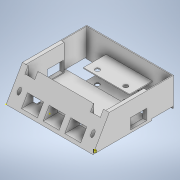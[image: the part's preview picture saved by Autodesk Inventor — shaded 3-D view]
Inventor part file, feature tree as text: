
AUTODESK INVENTOR PART (.ipt)
format: ipt  version: 2021 (Build 250183000, 183)  size: 445,952 bytes
history: native  units: mm
features: sketch x23, extrude x19, projected_geometry x2, other x1
ambient origin geometry x8: Origin, YZ Plane, XZ Plane, XY Plane, X Axis, Y Axis, Z Axis, Center Point
bodies: Body1 (feature_tree)
feature tree (45):
  other  "Sólido1"
  extrude  "Extrusion Base"  Depth=2.0mm TaperAngle=0.0deg
  extrude  "Extrusión Angulo parte de adelante"  Depth=100.0mm TaperAngle=0.0deg
  extrude  "parte trasera diseño"  Depth=4.5mm TaperAngle=0.0deg
  extrude  "Grado de inclinacion de 60.5 de parte delantera"  Depth=4.0mm TaperAngle=0.0deg
  extrude  "Lateral derecha de diseño"  Depth=103.25mm TaperAngle=0.0deg
  extrude  "Lateral izquierda diseño"  Depth=7.5mm
  extrude  "Extrusion capa parte delantera"  Depth=7.5mm
  extrude  "Extrusión huecos tornillos parte delantera"  Depth=3.0mm
  extrude  "Extrusión sensores laterales"  Depth=12.0mm
  extrude  "Extrusión sensores delanteros"  Depth=18.0mm
  extrude  "Extrusión arreglo sensores"  Depth=1.0mm
  extrude  "Extrusión desnivel sensores"  Depth=1.0mm
  sketch  "Boceto placa"  dims[d219=87.0mm d220=21.0mm d221=12.0mm d222=23.0mm d223=98.0mm d224=7.5mm d225=7.5mm d226=79.5mm d229=2.1mm d230=9.0mm d231=11.0mm d232=16.0mm d235=1.0mm d236=3.6mm d239=2.1mm d241=1.3mm d242=5.0mm d243=36.0mm d244=9.5mm d245=5.0mm d246=17.0mm d247=10.0mm d252=8.7mm d254=4.3mm d255=4.0mm d256=11.0mm d257=54.0mm d258=2.85mm d259=11.0mm d262=2.2mm d263=1.3mm d264=4.3mm d265=85.25mm d266=0.0mm d268=2.0mm d269=0.0mm d270=2.15mm d271=1.0mm d278=1.0mm d279=0.0mm d281=28.5mm d282=1.0mm d283=0.0mm d284=28.5mm d285=1.0mm d286=0.0mm d289=3.0mm d290=0.0mm d291=1.0mm d292=0.0mm d293=13.5mm d294=1.0mm d295=0.0mm d296=0.0mm d297=25.75mm d298=0.0mm d299=25.75mm d300=0.0mm d105=0.5mm d106=0.872665mm d107=0.5mm d108=0.872665mm d248=0.5mm d249=0.872665mm d250=0.5mm d251=0.872665mm d253=0.872665mm d272=0.5mm d273=0.872665mm d301=0.5mm d302=0.872665mm d303=0.5mm d304=0.872665mm]
  extrude  "Extrusión35"  Depth=18.0mm
  extrude  "Extrusión36"  Depth=6.4mm
  extrude  "Extrusión37"  Depth=18.0mm
  sketch  "Boceto52"  dims[d153=1.0mm d154=18.0mm]
  extrude  "Extrusión39"  Depth=12.0mm TaperAngle=0.0deg
  sketch  "Boceto54"  dims[d167=63.5mm d168=26.5mm]
  extrude  "Extrusión40"  Depth=63.5mm
  extrude  "Extrusión41"  Depth=10.0mm
  extrude  "Extrusión42"  Depth=3.5mm
  sketch  "Boceto58"  dims[d180=9.069006mm]
  sketch  "Boceto59"  dims[d210=0.0mm]
  sketch  "Boceto2"  dims[d6=3.5mm d22=2.0mm d23=0.0mm]
  sketch  "Boceto4"  dims[d24=20.935224mm d25=100.0mm d26=0.0mm]
  sketch  "Boceto5"  dims[d27=4.5mm d28=0.1mm d29=0.0mm]
  sketch  "Boceto10"  dims[d52=4.0mm d53=0.0mm d54=4.0mm d55=0.0mm]
  sketch  "Boceto11"  dims[d59=10.480702mm d60=103.25mm d61=0.0mm]
  projected_geometry  "Contorno proyectado1"
  sketch  "Boceto13"  dims[d65=93.0mm d66=0.0mm d67=7.5mm]
  sketch  "Boceto15"  dims[d68=7.5mm d69=3.5mm]
  projected_geometry  "Contorno proyectado2"
  sketch  "Boceto17"  dims[d70=90.25mm d71=0.0mm d131=3.0mm]
  sketch  "Boceto27"  dims[d132=18.0mm d133=12.0mm]
  sketch  "Boceto39"  dims[d134=98.25mm d135=0.0mm d144=18.0mm]
  sketch  "Boceto40"  dims[d145=12.0mm d146=1.0mm]
  sketch  "Boceto48"  dims[d147=11.5mm d148=1.0mm]
  sketch  "Boceto49"  dims[d149=12.0mm d150=18.0mm]
  sketch  "Boceto50"  dims[d151=6.4mm d152=6.4mm]
  sketch  "Boceto53"  dims[d155=12.0mm d156=19.25mm d157=0.0mm]
  sketch  "Boceto55"  dims[d172=84.0mm d176=10.0mm]
  sketch  "Boceto56"  dims[d177=3.993mm d178=3.5mm]
  sketch  "Boceto57"  dims[d179=35.5mm]
